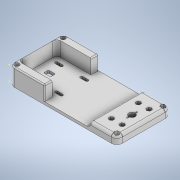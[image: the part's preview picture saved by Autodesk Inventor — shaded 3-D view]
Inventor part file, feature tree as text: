
AUTODESK INVENTOR PART (.ipt)
format: ipt  version: 2021 (Build 250183000, 183)  size: 784,384 bytes
history: native  units: mm
features: extrude x13, sketch x12, fillet x6, hole x2
ambient origin geometry x8: Origin, YZ Plane, XZ Plane, XY Plane, X Axis, Y Axis, Z Axis, Center Point
bodies: Solid1 (feature_tree)
feature tree (33):
  extrude  "Extrusion1"  Depth=2.0mm
  fillet  "Fillet3"  Radius=5.0mm
  hole  "Hole2"  [1 undecoded]
  hole  "Otwór3"  [1 undecoded]
  extrude  "Wyciągnięcie proste7"  Depth=2.0mm
  extrude  "Wyciągnięcie proste8"  Depth=2.0mm
  extrude  "Wyciągnięcie proste9"  Depth=2.0mm
  extrude  "Wyciągnięcie proste10"  TaperAngle=0.0deg  [1 undecoded]
  fillet  "Zaokrąglenie4"  Radius=7.0mm
  fillet  "Zaokrąglenie5"  Radius=7.0mm
  fillet  "Zaokrąglenie6"  Radius=72.0mm
  extrude  "Wyciągnięcie proste13"  Depth=2.0mm
  extrude  "Wyciągnięcie proste14"  Depth=2.0mm
  extrude  "Wyciągnięcie proste15"  Depth=10.0mm TaperAngle=0.0deg
  extrude  "Wyciągnięcie proste16"  Depth=10.0mm TaperAngle=0.0deg
  sketch  "Szkic65"
  extrude  "Wyciągnięcie proste19"  Depth=2.0mm TaperAngle=0.0deg
  extrude  "Wyciągnięcie proste20"  Depth=2.0mm
  extrude  "Wyciągnięcie proste21"  Depth=2.0mm
  extrude  "Wyciągnięcie proste22"  Depth=2.0mm
  fillet  "Zaokrąglenie10"  Radius=5.0mm
  sketch  "Szkic73"
  fillet  "Zaokrąglenie11"  Radius=3.0mm
  sketch  "Szkic74"
  sketch  "Szkic75"
  sketch  "Sketch2"  dims[d0=200.0mm d1=100.0mm d2=5.0mm d3=0.0mm d31=10.0mm d32=200.0mm d33=100.0mm d34=7.0mm d35=7.0mm d36=7.0mm d37=7.0mm d38=5.0mm d39=6.0mm d40=4.0mm d41=2.0mm d42=90.0deg d43=18.0mm d44=0.0mm d82=200.0mm d83=100.0mm d84=100.0mm d85=50.0mm d86=50.0mm d87=38.45mm d88=25.0mm d89=7.5mm d90=3.75mm d91=1.0mm d92=180.0deg d93=12.0mm d94=2.0mm d95=2.0mm d96=10.0mm d97=1.0mm d98=20.0mm d99=50.0mm d100=5.0mm d101=6.0mm d102=4.0mm d103=2.0mm d104=90.0deg d105=8.0mm d106=20.594885mm d107=200.0mm d108=100.0mm d109=100.0mm d110=50.0mm d111=50.0mm d112=38.45mm d113=25.0mm d114=7.5mm d115=3.75mm d116=1.0mm d117=180.0deg d118=12.0mm d119=2.0mm d120=2.0mm d121=10.0mm d122=1.0mm d123=20.0mm d124=50.0mm d125=0.0mm d126=0.0mm d140=7.0mm d141=7.0mm d142=72.0mm d143=14.0mm d144=15.0mm d145=10.0mm d146=0.0mm d147=10.0mm d148=0.0mm d151=6.0mm d152=0.0mm d153=5.0mm d154=2.0mm d155=6.0mm d172=5.0mm d174=3.0mm d176=12.5mm d177=12.5mm d178=12.5mm d179=0.0mm d180=0.0mm d182=19.65mm d184=15.5mm d185=3.0mm d186=3.0mm d187=3.5mm d188=6.0mm d189=12.5mm d190=6.0mm d191=5.0mm d192=3.0mm d193=12.5mm d194=12.5mm d195=12.5mm d196=19.65mm d204=0.0mm d205=0.0mm d223=6.0mm d224=0.0mm d233=0.0mm d234=0.0mm d269=1.575mm d272=4.575mm d274=4.575mm d275=4.575mm d276=4.575mm d277=0.0mm d278=0.0mm d279=1.575mm d281=4.575mm d282=4.575mm d283=4.575mm d284=10.0mm d285=10.0mm d286=10.0mm d287=10.0mm d288=10.0mm d289=5.0mm d290=0.0mm d291=1.575mm d292=4.575mm d293=4.575mm d294=4.575mm d295=10.0mm d296=10.0mm d297=10.0mm d298=10.0mm d299=10.0mm d300=0.2mm d301=0.2mm d302=0.2mm d303=0.2mm d305=0.2mm d306=27.0mm d307=0.0mm d308=8.5mm d309=8.5mm d310=27.0mm d311=0.0mm d312=2.0mm d313=2.0mm d65=0.5mm d66=0.872665mm d67=0.5mm d68=0.872665mm d80=0.5mm d81=0.872665mm d127=0.5mm d128=0.872665mm d129=0.5mm d130=0.872665mm d131=0.5mm d132=0.872665mm]
  sketch  "Szkic17"
  sketch  "Szkic20"
  sketch  "Szkic43"
  sketch  "Szkic44"
  sketch  "Szkic70"
  sketch  "Szkic71"
  sketch  "Szkic72"
note: 3 required parameter values undecoded (feature->parameter linkage not recoverable at this tier; creation-order binding heuristic only, values carry confidence <= 0.55)
